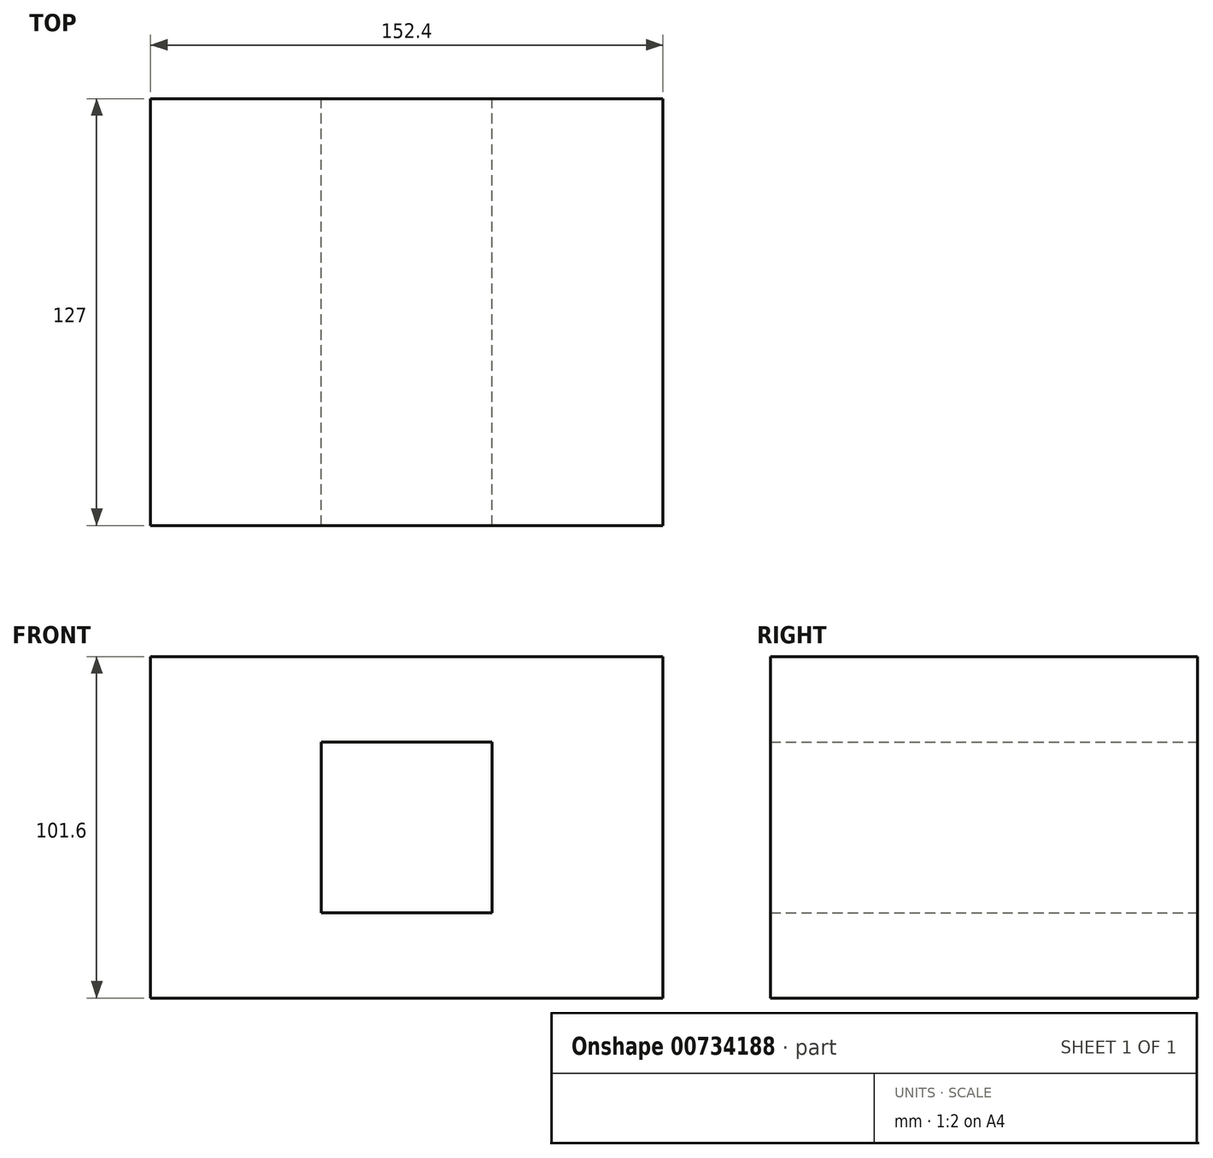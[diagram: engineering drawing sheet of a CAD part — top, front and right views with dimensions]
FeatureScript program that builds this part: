
annotation { "Feature Type Name" : "Feature", "Feature Type Description" : "" }
export const myFeature = defineFeature(function(context is Context, id is Id, definition is map)
    precondition{}
    {
        {
            var Q0;
            Q0=qCreatedBy(makeId("Front.planeOp"),FACE);
            var sketch = newSketch(context, id + "F0", { "sketchPlane" : qUnion([Q0])});
            skLineSegment(sketch, "E0", {"start": v(-43.5, 101.6) * mm, "end": v(108.9, 101.6) * mm});
            skLineSegment(sketch, "E1", {"start": v(108.9, 101.6) * mm, "end": v(108.9, 0) * mm});
            skLineSegment(sketch, "E2", {"start": v(108.9, 0) * mm, "end": v(-43.5, 0) * mm});
            skLineSegment(sketch, "E3", {"start": v(-43.5, 0) * mm, "end": v(-43.5, 101.6) * mm});
            skLineSegment(sketch, "E4", {"start": v(58.1, 25.4) * mm, "end": v(7.3, 25.4) * mm});
            skLineSegment(sketch, "E5", {"start": v(7.3, 25.4) * mm, "end": v(7.3, 76.2) * mm});
            skLineSegment(sketch, "E6", {"start": v(7.3, 76.2) * mm, "end": v(58.1, 76.2) * mm});
            skLineSegment(sketch, "E7", {"start": v(58.1, 76.2) * mm, "end": v(58.1, 25.4) * mm});
            skSolve(sketch);
        }
        {
            var Q0;
            Q0=makeQuery(id+"F0.imprint","IMPRINT",FACE,{"disambiguationData":[TD([[makeQuery(id+"F0.imprint","IMPRINT",EDGE,{"derivedFrom":sQuery(id+"F0.wireOp",EDGE,"E0")}),-1.0]])]});
            extrude(context, id + "F1", {"entities" : qUnion([Q0]), "depth" : 127 * mm, "offsetDistance" : 25.4 * mm});
        }
    });
